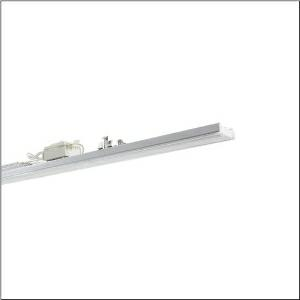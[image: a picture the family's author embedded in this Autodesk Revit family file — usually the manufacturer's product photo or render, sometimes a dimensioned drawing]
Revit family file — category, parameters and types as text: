
# Revit family: licross_21_recessed_mo_51te18vn48xg
name_source: partatom
category: Lighting Fixtures
units: mm (PartAtom-declared; Revit-internal decimal feet)

## family parameters
Cut with Voids When Loaded = No
Host = Face
Light Source = No
Part Type = Normal
Room Calculation Point = No
Round Connector Dimension = Use Diameter
Shared = No

## types (1)
- --- (1 x LED, 8000 lm, 44.7 W, 4000K)
    Apparent Load = 45 VA
    CIE Flux Codes = 83 96 99 100 100
    Color Rendering = 80
    Color Temperature = 4000K
    Default Elevation = 1800 mm
    Description = Licross 21 Recessed MO, luminaire insert, of sheet steel, galvanised, coil coated, white, length: 1.500mm, width: 66mm, height: 67mm, LED rated luminous flux: 8.000lm, light colour: 840, SDCM (Standard Deviation of Colour Matching)MacAdam ≤ 2 SDCM (initial), control gear: DALI 2, CLO, with plug, 5-pole, with phase selection, mains connection: 220..240V, AC, 50/60Hz, start of lifetime: 45W, end of service life: 49W, internal wiring halogen-free, primary light control with lens, of plastic, primary optical cover: cover, of PMMA, light emission: direct distribution, primary light characteristic: symmetric, protection rating (complete): IP54, insulation class (complete): insulation class I (protective earthing), certification: CE, ENEC, VDE, UKCA, protection symbol: D if used in an environment with non-conductive dust loads with corresponding accessories, impact resistance: IK06, permissible ambient temperature for indoor applications: -25..+35°C, corresponds to IFS (International Featured Standards) requirements for safety and quality in the food industry, reducing of maximum allowable ambient temperature of 5°C with ceiling mounting, LABS conformity tested according to VDMA 24364:2018-05, The light source and the operating device comply with the requirements of the Ecodesign Regulation (EU) 2019/2020 and are replaceable in accordance with this regulation, packaging unit: 1 piece
    Height = 58 mm
    Lamp = 1 x LED
    Lamp Light Flux = 8000 lm
    Lamp Power = 44.7 W
    Lamp count = 1
    Length = 1500 mm
    Luminous efficacy = 179 lm/W
    Manufacturer = Siteco
    ModVariant = No
    Model = 51TE18VN48XG
    Mounting Place = Ceiling
    Mounting Type = Pendant
    Number of Poles = 1
    OnlyDefault = Yes
    Power Factor = 1
    Product Name = Licross 21 Recessed MO
    Product group = luminaire insert | ceiling pendant
    ProductGroupID = 901
    Protection Class = Protection class I
    Protection Degree = IP 54
    RLX_Detail_Level = 1
    RLX_Emergency_Light_Flux = 0 lm
    RLX_Emergency_Type = 0
    RLX_Emergency_Type_DB = No
    RlxData = <blob elided: 24805 chars, md5=e1dbd318>
    Socket = socket
    Standby Power = 0 W
    System Light Flux = 8000 lm
    System Power = 45 W
    Type Comments = factory setting: luminous flux: 100 % | dim-lin: 254 | 299 mA
    Type Image = l_1296930.jpg
    URL = http://relux.com
    VarID = @adj_092357
    Voltage = 0 V
    Weight = 0.00 kg
    Width = 66 mm

## geometry (parser evidence)
native form markers: Blend x4, Sweep x10
no freeform markers — native parametric forms only
